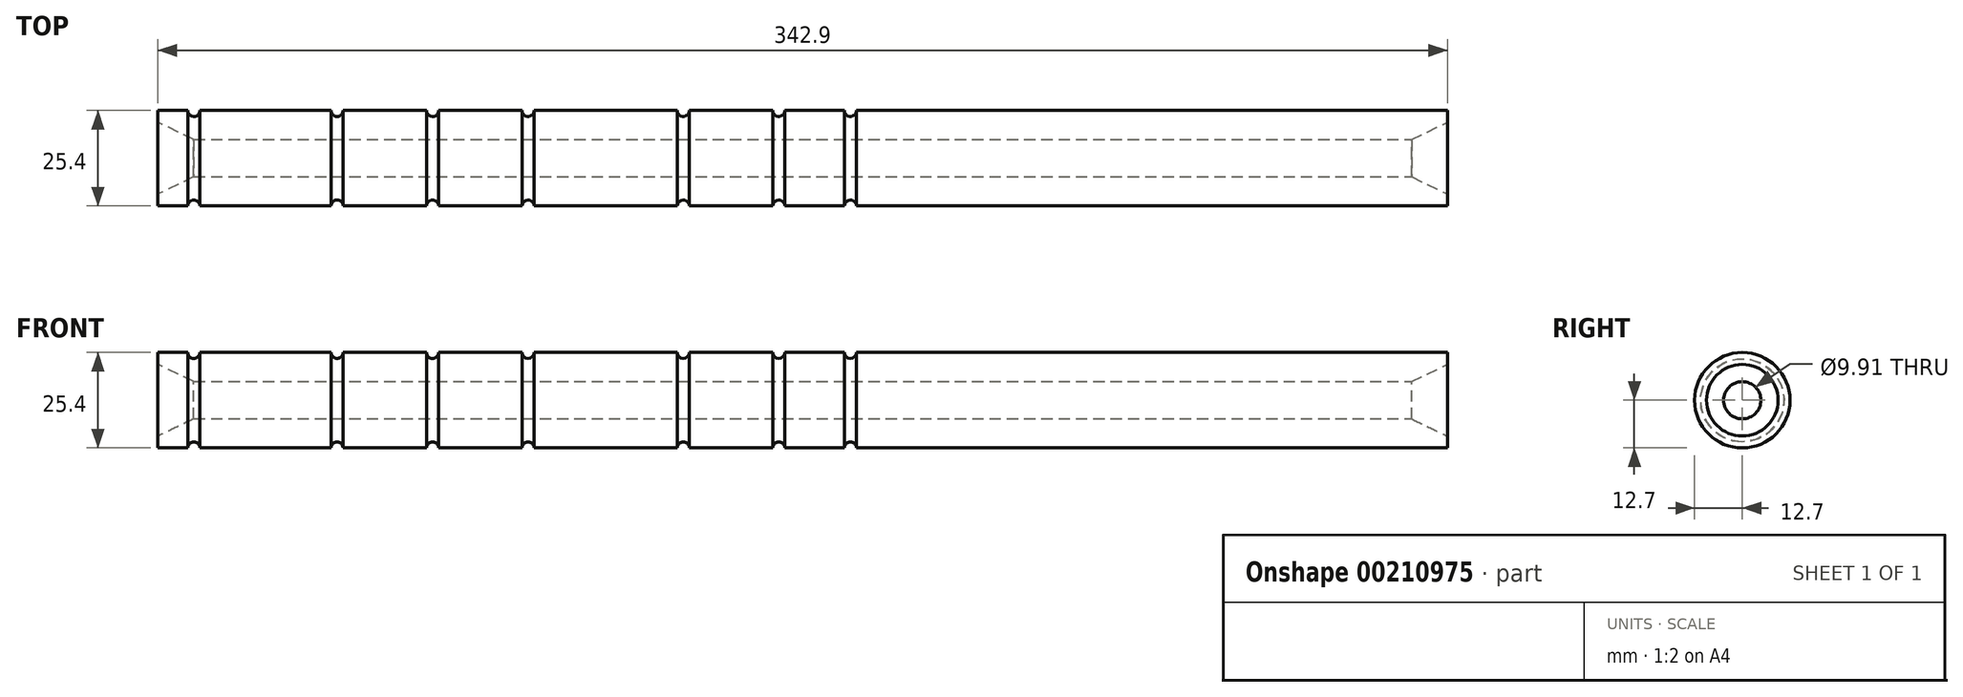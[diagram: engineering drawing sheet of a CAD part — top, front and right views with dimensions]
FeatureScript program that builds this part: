
annotation { "Feature Type Name" : "Feature", "Feature Type Description" : "" }
export const myFeature = defineFeature(function(context is Context, id is Id, definition is map)
    precondition{}
    {
        {
            var Q0;
            Q0=qCreatedBy(makeId("Front.planeOp"),FACE);
            var sketch = newSketch(context, id + "F0", { "sketchPlane" : qUnion([Q0])});
            skLineSegment(sketch, "E0", {"start": v(0, 0) * mm, "end": v(-342.9, 0) * mm});
            skLineSegment(sketch, "E1", {"start": v(0, 12.7) * mm, "end": v(-157.16, 12.7) * mm});
            skLineSegment(sketch, "E2", {"start": v(-9.53, 4.95) * mm, "end": v(-333.38, 4.95) * mm});
            skLineSegment(sketch, "E3", {"start": v(0, 12.7) * mm, "end": v(0, 9.53) * mm});
            skLineSegment(sketch, "E4", {"start": v(-342.9, 12.7) * mm, "end": v(-342.9, 9.52) * mm});
            skLineSegment(sketch, "E5", {"start": v(-342.9, 9.52) * mm, "end": v(-333.38, 4.95) * mm});
            skLineSegment(sketch, "E6", {"start": v(0, 9.53) * mm, "end": v(-9.53, 4.95) * mm});
            skArc(sketch, "E7", {"start": v(-334.96, 12.7) * mm, "mid": v(-333.38, 11.11) * mm, "end": v(-331.79, 12.7) * mm});
            skArc(sketch, "E8", {"start": v(-296.86, 12.7) * mm, "mid": v(-295.28, 11.11) * mm, "end": v(-293.69, 12.7) * mm});
            skArc(sketch, "E9", {"start": v(-271.46, 12.7) * mm, "mid": v(-269.88, 11.11) * mm, "end": v(-268.29, 12.7) * mm});
            skArc(sketch, "E10", {"start": v(-246.06, 12.7) * mm, "mid": v(-244.48, 11.11) * mm, "end": v(-242.89, 12.7) * mm});
            skArc(sketch, "E11", {"start": v(-204.79, 12.7) * mm, "mid": v(-203.2, 11.11) * mm, "end": v(-201.61, 12.7) * mm});
            skArc(sketch, "E12", {"start": v(-179.39, 12.7) * mm, "mid": v(-177.8, 11.11) * mm, "end": v(-176.21, 12.7) * mm});
            skArc(sketch, "E13", {"start": v(-160.34, 12.7) * mm, "mid": v(-158.75, 11.11) * mm, "end": v(-157.16, 12.7) * mm});
            skLineSegment(sketch, "E14.trimOffspring", {"start": v(-179.39, 12.7) * mm, "end": v(-201.61, 12.7) * mm});
            skLineSegment(sketch, "E15.trimOffspring", {"start": v(-204.79, 12.7) * mm, "end": v(-242.89, 12.7) * mm});
            skLineSegment(sketch, "E16.trimOffspring", {"start": v(-160.34, 12.7) * mm, "end": v(-176.21, 12.7) * mm});
            skLineSegment(sketch, "E17.trimOffspring", {"start": v(-334.96, 12.7) * mm, "end": v(-342.9, 12.7) * mm});
            skLineSegment(sketch, "E18.trimOffspring", {"start": v(-296.86, 12.7) * mm, "end": v(-331.79, 12.7) * mm});
            skLineSegment(sketch, "E19.trimOffspring", {"start": v(-271.46, 12.7) * mm, "end": v(-293.69, 12.7) * mm});
            skLineSegment(sketch, "E20.trimOffspring", {"start": v(-246.06, 12.7) * mm, "end": v(-268.29, 12.7) * mm});
            skSolve(sketch);
        }
        {
            var Q0;
            Q0=makeQuery(id+"F0.imprint","IMPRINT",FACE,{"disambiguationData":[TD([[makeQuery(id+"F0.imprint","IMPRINT",EDGE,{"derivedFrom":sQuery(id+"F0.wireOp",EDGE,"E1")}),1.0]])]});
            var Q1;
            Q1=sQuery(id+"F0.wireOp",EDGE,"E0");
            revolve(context, id + "F1", {"entities" : qUnion([Q0]), "axis" : qUnion([Q1]), "revolveType" : RevolveType.FULL});
        }
    });
